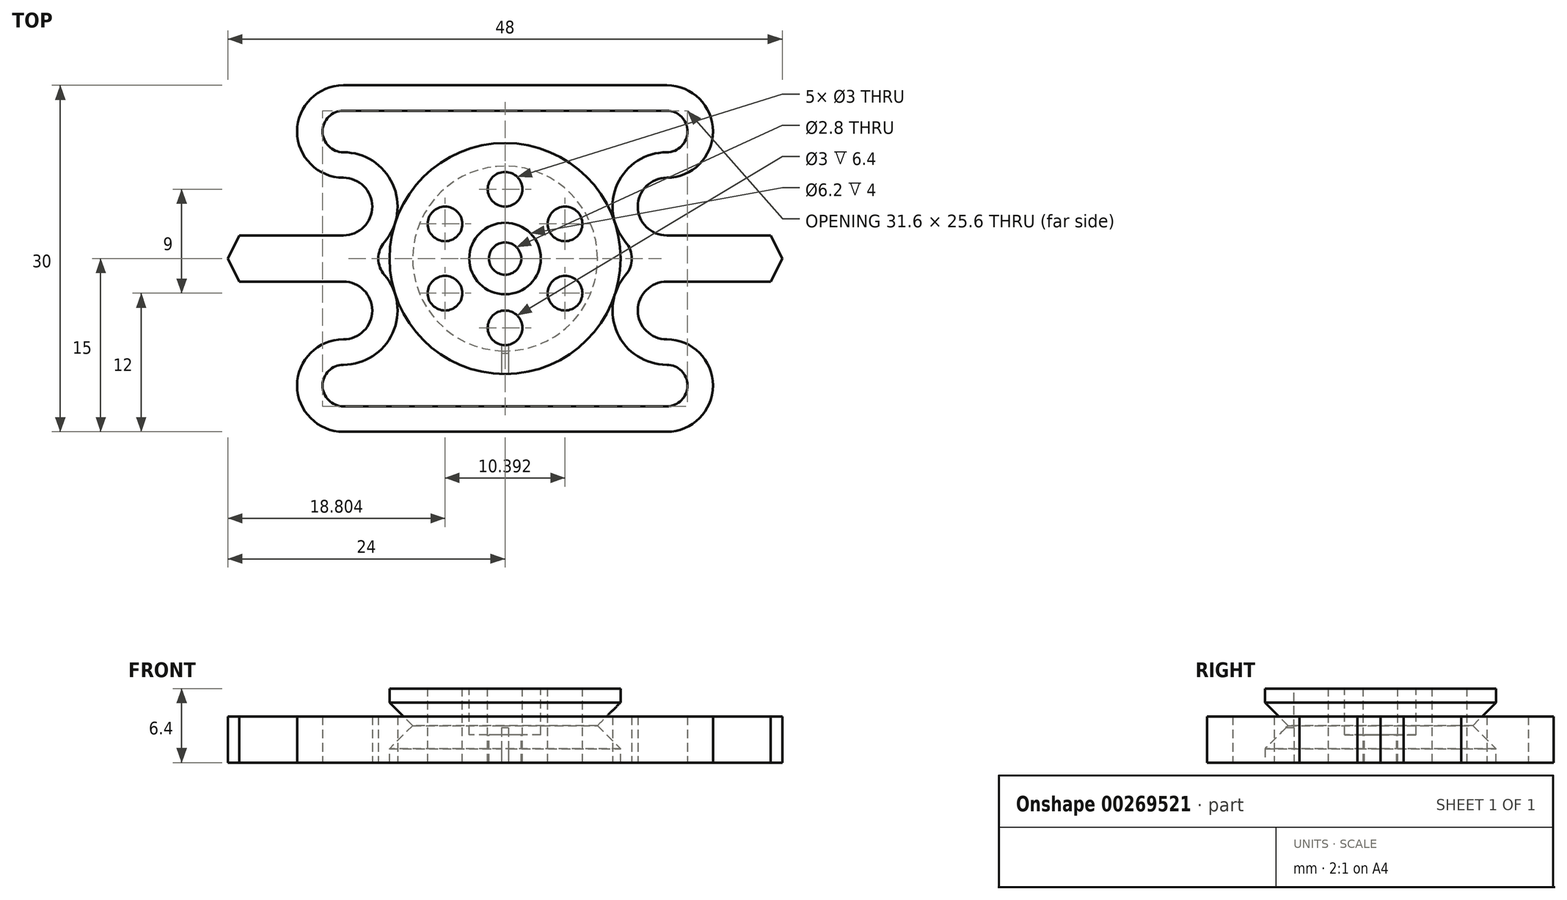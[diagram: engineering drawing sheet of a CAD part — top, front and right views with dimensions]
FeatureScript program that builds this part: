
annotation { "Feature Type Name" : "Feature", "Feature Type Description" : "" }
export const myFeature = defineFeature(function(context is Context, id is Id, definition is map)
    precondition{}
    {
        {
            var Q0;
            Q0=qCreatedBy(makeId("Top.planeOp"),FACE);
            var sketch = newSketch(context, id + "F0", { "sketchPlane" : qUnion([Q0])});
            skLineSegment(sketch, "E0", {"start": v(-24, 0) * mm, "end": v(24, 0) * mm, "construction": true});
            skLineSegment(sketch, "E1", {"start": v(-24, 0) * mm, "end": v(-23, 2) * mm});
            skLineSegment(sketch, "E2", {"start": v(-23, 2) * mm, "end": v(-14, 2) * mm});
            skLineSegment(sketch, "E3", {"start": v(-14, 15) * mm, "end": v(0, 15) * mm});
            skLineSegment(sketch, "E4", {"start": v(-14, 15) * mm, "end": v(-14, 2) * mm, "construction": true});
            skArc(sketch, "E5", {"start": v(-14, 2) * mm, "mid": v(-11.5, 4.5) * mm, "end": v(-14, 7) * mm});
            skArc(sketch, "E6", {"start": v(-14, 7) * mm, "mid": v(-18, 11) * mm, "end": v(-14, 15) * mm});
            skLineSegment(sketch, "E7.MirrorCS", {"start": v(14, 15) * mm, "end": v(0, 15) * mm});
            skArc(sketch, "E8.MirrorCS", {"start": v(14, 7) * mm, "mid": v(18, 11) * mm, "end": v(14, 15) * mm});
            skArc(sketch, "E9.MirrorCS", {"start": v(14, 2) * mm, "mid": v(11.5, 4.5) * mm, "end": v(14, 7) * mm});
            skLineSegment(sketch, "E10.MirrorCS", {"start": v(23, 2) * mm, "end": v(14, 2) * mm});
            skLineSegment(sketch, "E11.MirrorCS", {"start": v(24, 0) * mm, "end": v(23, 2) * mm});
            skLineSegment(sketch, "E12.MirrorCS", {"start": v(-24, 0) * mm, "end": v(-23, -2) * mm});
            skLineSegment(sketch, "E13.MirrorCS", {"start": v(-23, -2) * mm, "end": v(-14, -2) * mm});
            skArc(sketch, "E14.MirrorCS", {"start": v(-14, -2) * mm, "mid": v(-11.5, -4.5) * mm, "end": v(-14, -7) * mm});
            skArc(sketch, "E15.MirrorCS", {"start": v(-14, -7) * mm, "mid": v(-18, -11) * mm, "end": v(-14, -15) * mm});
            skLineSegment(sketch, "E16.MirrorCS", {"start": v(-14, -15) * mm, "end": v(0, -15) * mm});
            skLineSegment(sketch, "E17.MirrorCS", {"start": v(14, -15) * mm, "end": v(0, -15) * mm});
            skArc(sketch, "E18.MirrorCS", {"start": v(14, -7) * mm, "mid": v(18, -11) * mm, "end": v(14, -15) * mm});
            skArc(sketch, "E19.MirrorCS", {"start": v(14, -2) * mm, "mid": v(11.5, -4.5) * mm, "end": v(14, -7) * mm});
            skLineSegment(sketch, "E20.MirrorCS", {"start": v(23, -2) * mm, "end": v(14, -2) * mm});
            skLineSegment(sketch, "E21.MirrorCS", {"start": v(24, 0) * mm, "end": v(23, -2) * mm});
            skArc(sketch, "E22.0", {"start": v(-10.44, -1.43) * mm, "mid": v(-9.73, -6.46) * mm, "end": v(-14, -9.2) * mm});
            skArc(sketch, "E22.1", {"start": v(14, 9.2) * mm, "mid": v(15.8, 11) * mm, "end": v(14, 12.8) * mm});
            skLineSegment(sketch, "E22.2", {"start": v(14, 12.8) * mm, "end": v(0.51, 12.8) * mm});
            skLineSegment(sketch, "E22.3", {"start": v(-14, 12.8) * mm, "end": v(0.51, 12.8) * mm});
            skArc(sketch, "E22.4", {"start": v(-14, 9.2) * mm, "mid": v(-15.8, 11) * mm, "end": v(-14, 12.8) * mm});
            skArc(sketch, "E22.5", {"start": v(10.44, 1.43) * mm, "mid": v(9.73, 6.46) * mm, "end": v(14, 9.2) * mm});
            skArc(sketch, "E22.6", {"start": v(-10.44, 1.43) * mm, "mid": v(-9.73, 6.46) * mm, "end": v(-14, 9.2) * mm});
            skArc(sketch, "E22.7", {"start": v(10.44, -1.43) * mm, "mid": v(9.73, -6.46) * mm, "end": v(14, -9.2) * mm});
            skArc(sketch, "E22.8", {"start": v(14, -9.2) * mm, "mid": v(15.8, -11) * mm, "end": v(14, -12.8) * mm});
            skLineSegment(sketch, "E22.9", {"start": v(14, -12.8) * mm, "end": v(0, -12.8) * mm});
            skLineSegment(sketch, "E22.10", {"start": v(-14, -12.8) * mm, "end": v(0, -12.8) * mm});
            skArc(sketch, "E22.11", {"start": v(-14, -9.2) * mm, "mid": v(-15.8, -11) * mm, "end": v(-14, -12.8) * mm});
            skPoint(sketch, "E23.visualSharp", {"position": v(-12.64, 0) * mm});
            skArc(sketch, "E23.filletArc", {"start": v(-10.44, 1.43) * mm, "mid": v(-10.97, 0) * mm, "end": v(-10.44, -1.43) * mm});
            skPoint(sketch, "E24.visualSharp", {"position": v(12.64, 0) * mm});
            skArc(sketch, "E24.filletArc", {"start": v(10.44, -1.43) * mm, "mid": v(10.97, 0) * mm, "end": v(10.44, 1.43) * mm});
            skSolve(sketch);
        }
        {
            var Q0;
            Q0=makeQuery(id+"F0.imprint","IMPRINT",FACE,{"disambiguationData":[TD([[makeQuery(id+"F0.imprint","IMPRINT",EDGE,{"derivedFrom":sQuery(id+"F0.wireOp",EDGE,"E1")}),-1.0]])]});
            extrude(context, id + "F1", {"entities" : qUnion([Q0]), "depth" : 4 * mm});
        }
        {
            var Q0;
            Q0=qCreatedBy(makeId("Front.planeOp"),FACE);
            var sketch = newSketch(context, id + "F2", { "sketchPlane" : qUnion([Q0])});
            skLineSegment(sketch, "E25", {"start": v(0, 0) * mm, "end": v(10, 0) * mm});
            skLineSegment(sketch, "E26", {"start": v(10, 0) * mm, "end": v(10, 1.2) * mm});
            skLineSegment(sketch, "E27", {"start": v(10, 1.2) * mm, "end": v(10, 5.2) * mm, "construction": true});
            skLineSegment(sketch, "E28", {"start": v(10, 5.2) * mm, "end": v(10, 6.4) * mm});
            skLineSegment(sketch, "E29", {"start": v(10, 6.4) * mm, "end": v(0, 6.4) * mm});
            skLineSegment(sketch, "E30", {"start": v(0, 6.4) * mm, "end": v(0, 0) * mm});
            skLineSegment(sketch, "E31", {"start": v(10, 3.2) * mm, "end": v(8, 3.2) * mm, "construction": true});
            skLineSegment(sketch, "E32", {"start": v(8, 3.2) * mm, "end": v(10, 5.2) * mm});
            skLineSegment(sketch, "E33", {"start": v(10, 1.2) * mm, "end": v(8, 3.2) * mm});
            skSolve(sketch);
        }
        {
            var Q0;
            Q0=makeQuery(id+"F2.imprint","IMPRINT",FACE,{"disambiguationData":[TD([[makeQuery(id+"F2.imprint","IMPRINT",EDGE,{"derivedFrom":sQuery(id+"F2.wireOp",EDGE,"E25")}),1.0]])]});
            var Q1;
            Q1=sQuery(id+"F2.wireOp",EDGE,"E30");
            revolve(context, id + "F3", {"entities" : qUnion([Q0]), "axis" : qUnion([Q1]), "revolveType" : RevolveType.FULL});
        }
        {
            var Q0;
            Q0=makeQuery(id+"F3.opRevolve","SWEPT_FACE",FACE,{"disambiguationData":[OSD([sQuery(id+"F2.wireOp",EDGE,"E29")])]});
            var sketch = newSketch(context, id + "F4", { "sketchPlane" : qUnion([Q0])});
            skCircle(sketch, "E34", {"center": v(0, 0) * mm, "radius": 1.4 * mm});
            skCircle(sketch, "E35", {"center": v(0, 6) * mm, "radius": 1.5 * mm});
            skCircle(sketch, "E36.1.0", {"center": v(-5.2, 3) * mm, "radius": 1.5 * mm});
            skCircle(sketch, "E36.2.0", {"center": v(-5.2, -3) * mm, "radius": 1.5 * mm});
            skCircle(sketch, "E36.3.0", {"center": v(0, -6) * mm, "radius": 1.5 * mm});
            skCircle(sketch, "E36.4.0", {"center": v(5.2, -3) * mm, "radius": 1.5 * mm});
            skCircle(sketch, "E36.5.0", {"center": v(5.2, 3) * mm, "radius": 1.5 * mm});
            skCircle(sketch, "E37", {"center": v(0, 0) * mm, "radius": 3.1 * mm});
            skCircle(sketch, "E38.0", {"center": v(0, 0) * mm, "radius": 10 * mm});
            skSolve(sketch);
        }
        {
            var Q0;
            {var subQ0=sQuery(id+"F4.wireOp",EDGE,"E35");var subQ1=makeQuery(id+"F4.imprint","INTERSECT",VERTEX,{"derivedFrom":[subQ0,sQuery(id+"F4.wireOp",EDGE,"mKZ1OoVz-9I2j-gmvt-k5IN-Mte78Ou1n9wl")]});Q0=makeQuery(id+"F4.imprint","IMPRINT",FACE,{"disambiguationData":[TD([[makeQuery(id+"F4.imprint","IMPRINT",EDGE,{"disambiguationData":[TD([[subQ1,-1.0]])],"derivedFrom":subQ0}),1.0]])]});}
            var Q1;
            Q1=makeQuery(id+"F4.imprint","IMPRINT",FACE,{"disambiguationData":[TD([[makeQuery(id+"F4.imprint","IMPRINT",EDGE,{"derivedFrom":sQuery(id+"F4.wireOp",EDGE,"E36.5.0")}),1.0]])]});
            var Q2;
            Q2=makeQuery(id+"F4.imprint","IMPRINT",FACE,{"disambiguationData":[TD([[makeQuery(id+"F4.imprint","IMPRINT",EDGE,{"derivedFrom":sQuery(id+"F4.wireOp",EDGE,"E36.4.0")}),1.0]])]});
            var Q3;
            Q3=makeQuery(id+"F4.imprint","IMPRINT",FACE,{"disambiguationData":[TD([[makeQuery(id+"F4.imprint","IMPRINT",EDGE,{"derivedFrom":sQuery(id+"F4.wireOp",EDGE,"E36.3.0")}),1.0]])]});
            var Q4;
            Q4=makeQuery(id+"F4.imprint","IMPRINT",FACE,{"disambiguationData":[TD([[makeQuery(id+"F4.imprint","IMPRINT",EDGE,{"derivedFrom":sQuery(id+"F4.wireOp",EDGE,"E36.2.0")}),1.0]])]});
            var Q5;
            Q5=makeQuery(id+"F4.imprint","IMPRINT",FACE,{"disambiguationData":[TD([[makeQuery(id+"F4.imprint","IMPRINT",EDGE,{"derivedFrom":sQuery(id+"F4.wireOp",EDGE,"E36.1.0")}),1.0]])]});
            var Q6;
            Q6=makeQuery(id+"F4.imprint","IMPRINT",FACE,{"disambiguationData":[TD([[makeQuery(id+"F4.imprint","IMPRINT",EDGE,{"derivedFrom":sQuery(id+"F4.wireOp",EDGE,"E34")}),1.0]])]});
            var Q7;
            Q7=makeQuery(id+"F4.imprint","IMPRINT",FACE,{"disambiguationData":[TD([[makeQuery(id+"F4.imprint","IMPRINT",EDGE,{"derivedFrom":sQuery(id+"F4.wireOp",EDGE,"E35")}),1.0]])]});
            extrude(context, id + "F5", {"entities" : qUnion([Q0, Q1, Q2, Q3, Q4, Q5, Q6, Q7]), "operationType" : NewBodyOperationType.REMOVE, "endBound" : BoundingType.THROUGH_ALL, "oppositeDirection" : true, "depth" : 25 * mm});
        }
        {
            var Q0;
            Q0=makeQuery(id+"F4.imprint","IMPRINT",FACE,{"disambiguationData":[TD([[makeQuery(id+"F4.imprint","IMPRINT",EDGE,{"derivedFrom":sQuery(id+"F4.wireOp",EDGE,"E34")}),-1.0]])]});
            extrude(context, id + "F6", {"entities" : qUnion([Q0]), "operationType" : NewBodyOperationType.REMOVE, "oppositeDirection" : true, "depth" : 4 * mm});
        }
        {
            var Q0;
            Q0=makeQuery(id+"F3.opRevolve","SWEPT_FACE",FACE,{"disambiguationData":[OSD([sQuery(id+"F2.wireOp",EDGE,"E25")])]});
            var sketch = newSketch(context, id + "F7", { "sketchPlane" : qUnion([Q0])});
            skLineSegment(sketch, "E39", {"start": v(0.3, 7.47) * mm, "end": v(0.3, 10) * mm});
            skCircle(sketch, "E40.0", {"center": v(0, 0) * mm, "radius": 10 * mm});
            skCircle(sketch, "E41.0", {"center": v(0, 6) * mm, "radius": 1.5 * mm});
            skLineSegment(sketch, "E42.MirrorCS", {"start": v(-0.3, 7.47) * mm, "end": v(-0.3, 10) * mm});
            skSolve(sketch);
        }
        {
            var Q0;
            {var subQ0=sQuery(id+"F7.wireOp",EDGE,"E39");Q0=makeQuery(id+"F7.imprint","IMPRINT",FACE,{"disambiguationData":[TD([[makeQuery(id+"F7.imprint","IMPRINT",EDGE,{"derivedFrom":subQ0}),1.0]])]});}
            extrude(context, id + "F8", {"entities" : qUnion([Q0]), "operationType" : NewBodyOperationType.REMOVE, "oppositeDirection" : true, "depth" : 3 * mm});
        }
    });
